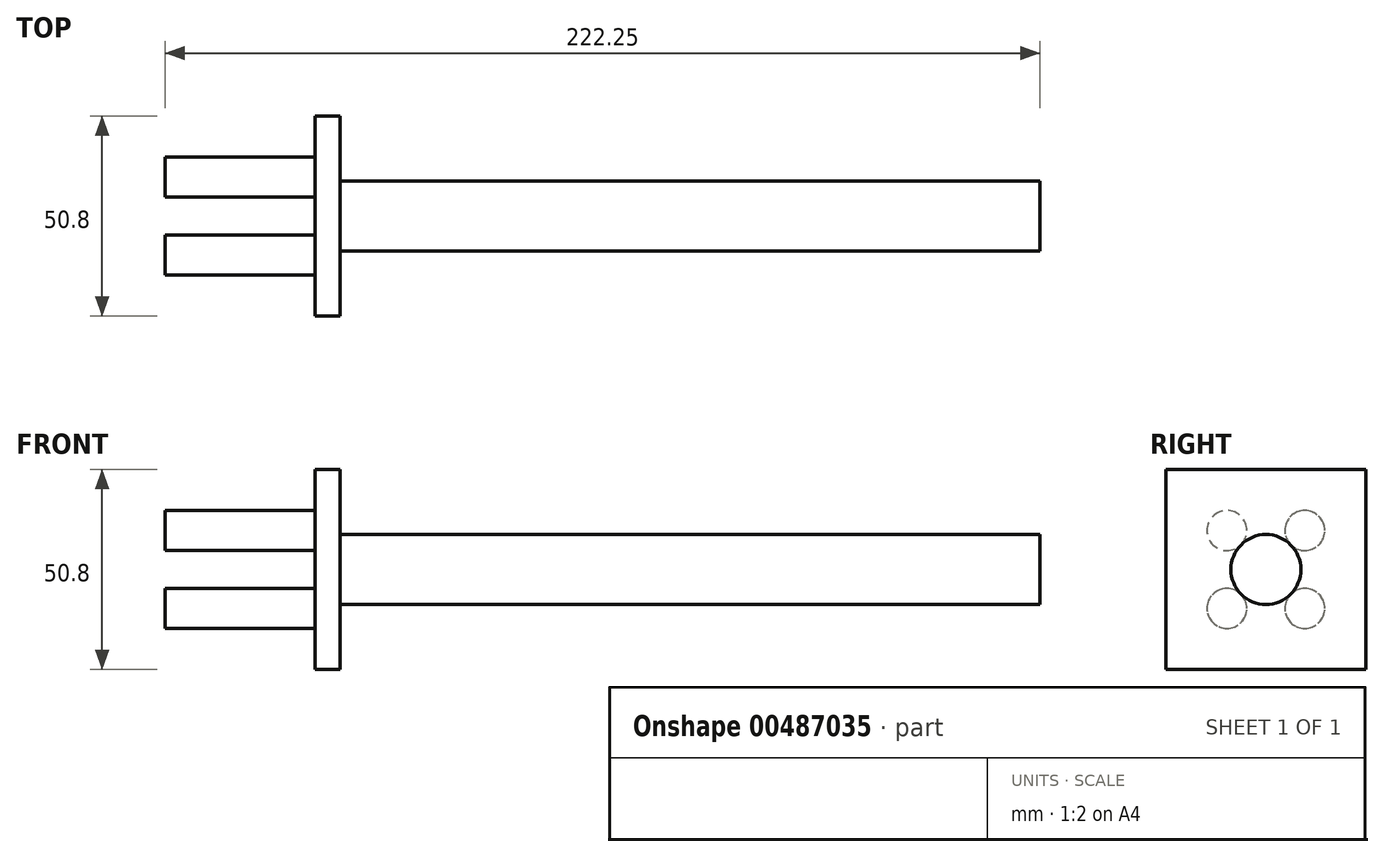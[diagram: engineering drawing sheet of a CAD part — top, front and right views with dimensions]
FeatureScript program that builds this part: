
annotation { "Feature Type Name" : "Feature", "Feature Type Description" : "" }
export const myFeature = defineFeature(function(context is Context, id is Id, definition is map)
    precondition{}
    {
        {
            var Q0;
            Q0=qCreatedBy(makeId("Right.planeOp"),FACE);
            var sketch = newSketch(context, id + "F0", { "sketchPlane" : qUnion([Q0])});
            skCircle(sketch, "E0", {"center": v(0, 0) * mm, "radius": 8.9 * mm});
            skSolve(sketch);
        }
        {
            var Q0;
            Q0 = qSketchRegion(id + "F0", true);
            extrude(context, id + "F1", {"entities" : qUnion([Q0]), "depth" : 177.8 * mm});
        }
        {
            var Q0;
            Q0=qCreatedBy(makeId("Right.planeOp"),FACE);
            var sketch = newSketch(context, id + "F2", { "sketchPlane" : qUnion([Q0])});
            skLineSegment(sketch, "E1.bottom", {"start": v(-25.4, -25.4) * mm, "end": v(25.4, -25.4) * mm});
            skLineSegment(sketch, "E1.top", {"start": v(-25.4, 25.4) * mm, "end": v(25.4, 25.4) * mm});
            skLineSegment(sketch, "E1.left", {"start": v(-25.4, -25.4) * mm, "end": v(-25.4, 25.4) * mm});
            skLineSegment(sketch, "E1.right", {"start": v(25.4, -25.4) * mm, "end": v(25.4, 25.4) * mm});
            skPoint(sketch, "E1.middle", {"position": v(0, 0) * mm});
            skSolve(sketch);
        }
        {
            var Q0;
            Q0 = qSketchRegion(id + "F2", true);
            extrude(context, id + "F3", {"entities" : qUnion([Q0]), "operationType" : NewBodyOperationType.ADD, "oppositeDirection" : true, "depth" : 6.35 * mm});
        }
        {
            var Q0;
            Q0=makeQuery(id+"F3.opExtrude","CAP_FACE",FACE,{"disambiguationData":[OSD([sQuery(id+"F2.wireOp",EDGE,"E1.bottom"),sQuery(id+"F2.wireOp",EDGE,"E1.top"),sQuery(id+"F2.wireOp",EDGE,"E1.left"),sQuery(id+"F2.wireOp",EDGE,"E1.right")])],"isStart":false});
            var sketch = newSketch(context, id + "F4", { "sketchPlane" : qUnion([Q0])});
            skCircle(sketch, "E2", {"center": v(9.88, 9.88) * mm, "radius": 5.08 * mm});
            skCircle(sketch, "E3", {"center": v(-9.88, 9.88) * mm, "radius": 5.08 * mm});
            skCircle(sketch, "E4", {"center": v(-9.88, -9.88) * mm, "radius": 5.08 * mm});
            skCircle(sketch, "E5", {"center": v(9.88, -9.88) * mm, "radius": 5.08 * mm});
            skLineSegment(sketch, "E6", {"start": v(-25.4, 25.4) * mm, "end": v(25.4, -25.4) * mm});
            skLineSegment(sketch, "E7", {"start": v(25.4, 25.4) * mm, "end": v(-25.4, -25.4) * mm});
            skSolve(sketch);
        }
        {
            var Q0;
            Q0 = qSketchRegion(id + "F4", true);
            extrude(context, id + "F5", {"entities" : qUnion([Q0]), "operationType" : NewBodyOperationType.ADD, "depth" : 38.1 * mm});
        }
    });
